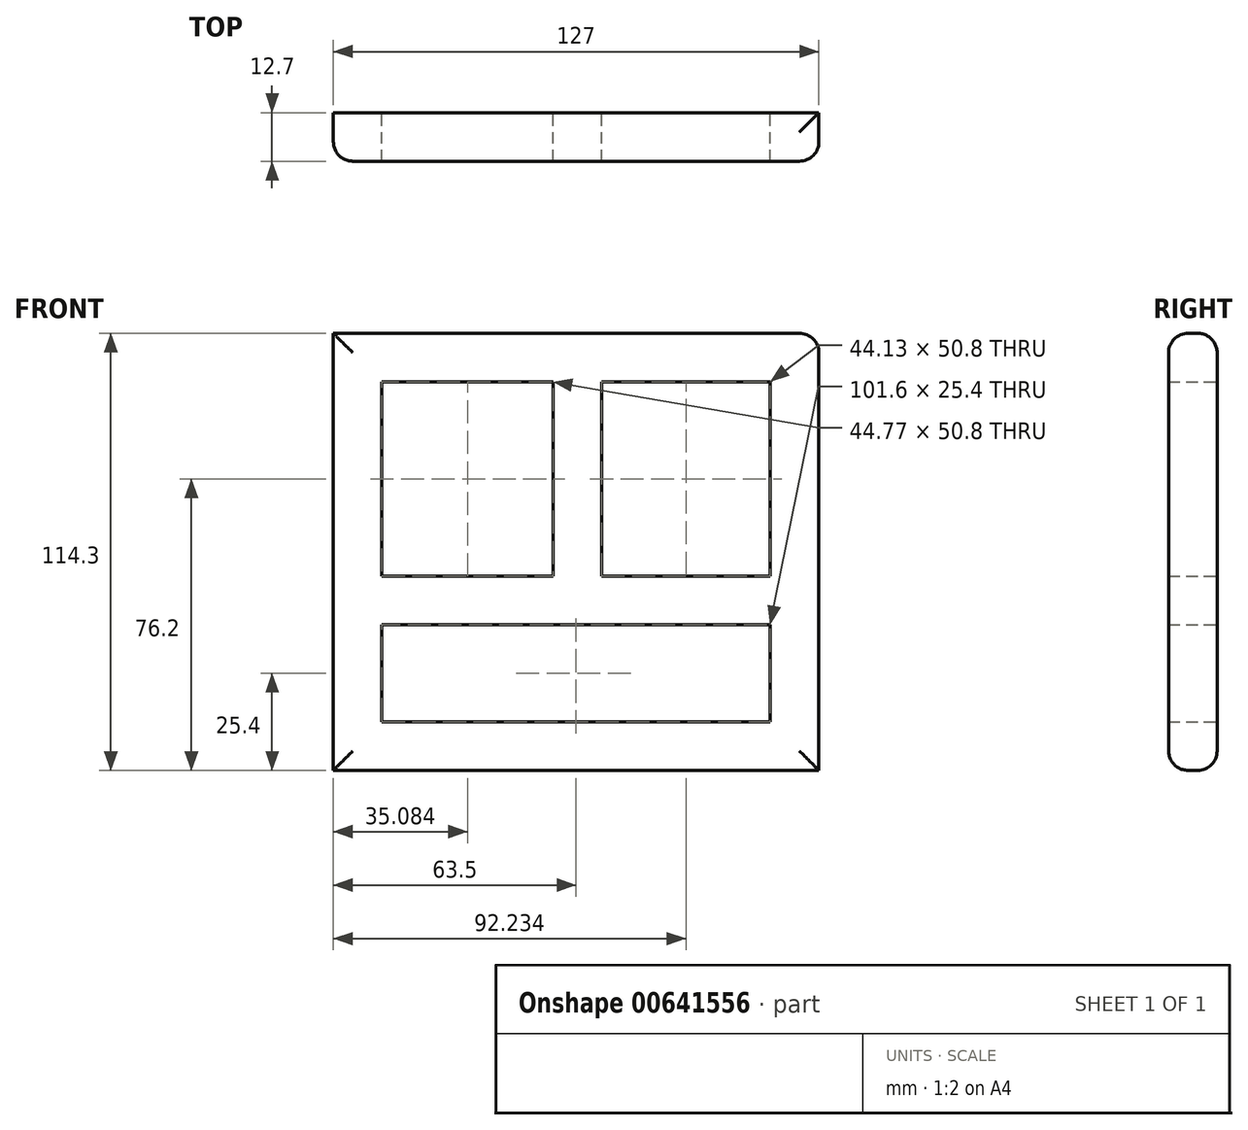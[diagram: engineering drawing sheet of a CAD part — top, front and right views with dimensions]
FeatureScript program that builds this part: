
annotation { "Feature Type Name" : "Feature", "Feature Type Description" : "" }
export const myFeature = defineFeature(function(context is Context, id is Id, definition is map)
    precondition{}
    {
        {
            var Q0;
            Q0=qCreatedBy(makeId("Front.planeOp"),FACE);
            var sketch = newSketch(context, id + "F0", { "sketchPlane" : qUnion([Q0])});
            skLineSegment(sketch, "E0.bottom", {"start": v(-63.5, -25.4) * mm, "end": v(63.5, -25.4) * mm});
            skLineSegment(sketch, "E0.top", {"start": v(-50.8, 25.4) * mm, "end": v(50.8, 25.4) * mm});
            skLineSegment(sketch, "E0.left", {"start": v(-63.5, -25.4) * mm, "end": v(-63.5, 25.4) * mm});
            skLineSegment(sketch, "E0.right", {"start": v(63.5, -25.4) * mm, "end": v(63.5, 25.4) * mm});
            skPoint(sketch, "E0.middle", {"position": v(0, 0) * mm});
            skLineSegment(sketch, "E1.bottom", {"start": v(-50.8, -12.7) * mm, "end": v(50.8, -12.7) * mm});
            skLineSegment(sketch, "E1.top", {"start": v(-50.8, 12.7) * mm, "end": v(50.8, 12.7) * mm});
            skLineSegment(sketch, "E1.left", {"start": v(-50.8, -12.7) * mm, "end": v(-50.8, 12.7) * mm});
            skLineSegment(sketch, "E1.right", {"start": v(50.8, -12.7) * mm, "end": v(50.8, 12.7) * mm});
            skLineSegment(sketch, "E2", {"start": v(-63.5, 25.4) * mm, "end": v(-63.5, 88.9) * mm});
            skLineSegment(sketch, "E3", {"start": v(-63.5, 88.9) * mm, "end": v(63.5, 88.9) * mm});
            skLineSegment(sketch, "E4", {"start": v(63.5, 88.9) * mm, "end": v(63.5, 25.4) * mm});
            skLineSegment(sketch, "E5", {"start": v(-50.8, 25.4) * mm, "end": v(-50.8, 76.2) * mm});
            skLineSegment(sketch, "E6", {"start": v(-50.8, 76.2) * mm, "end": v(50.8, 76.2) * mm});
            skLineSegment(sketch, "E7", {"start": v(50.8, 76.2) * mm, "end": v(50.8, 25.4) * mm});
            skLineSegment(sketch, "E8", {"start": v(-6.03, 25.4) * mm, "end": v(-6.03, 76.2) * mm});
            skLineSegment(sketch, "E9", {"start": v(-6.03, 76.2) * mm, "end": v(6.67, 76.2) * mm});
            skLineSegment(sketch, "E10", {"start": v(6.67, 76.2) * mm, "end": v(6.67, 25.4) * mm});
            skLineSegment(sketch, "E11", {"start": v(-50.8, 25.4) * mm, "end": v(-50.8, 12.7) * mm});
            skLineSegment(sketch, "E12", {"start": v(50.8, 25.4) * mm, "end": v(50.8, 12.7) * mm});
            skSolve(sketch);
        }
        {
            var Q0;
            Q0 = qSketchRegion(id + "F0", true);
            var Q1;
            Q1=makeQuery(id+"F0.imprint","IMPRINT",FACE,{"disambiguationData":[TD([[makeQuery(id+"F0.imprint","IMPRINT",EDGE,{"derivedFrom":sQuery(id+"F0.wireOp",EDGE,"E1.top")}),1.0]])]});
            var Q2;
            {var subQ0=sQuery(id+"F0.wireOp",EDGE,"E8");Q2=makeQuery(id+"F0.imprint","IMPRINT",FACE,{"disambiguationData":[TD([[makeQuery(id+"F0.imprint","IMPRINT",EDGE,{"derivedFrom":subQ0}),-1.0]])]});}
            extrude(context, id + "F1", {"entities" : qUnion([Q0, Q1, Q2]), "depth" : 12.7 * mm, "offsetDistance" : 25.4 * mm});
        }
        {
            var Q0;
            Q0=makeQuery(id+"F1.opExtrude","CAP_EDGE",EDGE,{"disambiguationData":[OSD([sQuery(id+"F0.wireOp",EDGE,"E3")])],"isStart":true});
            var Q1;
            Q1=makeQuery(id+"F1.opExtrude","CAP_EDGE",EDGE,{"disambiguationData":[OSD([sQuery(id+"F0.wireOp",EDGE,"E0.bottom")])],"isStart":true});
            var Q2;
            Q2=makeQuery(id+"F1.opExtrude","CAP_EDGE",EDGE,{"disambiguationData":[OSD([sQuery(id+"F0.wireOp",EDGE,"E0.right"),sQuery(id+"F0.wireOp",EDGE,"E4")])],"isStart":false});
            var Q3;
            Q3=makeQuery(id+"F1.opExtrude","SWEPT_EDGE",EDGE,{"disambiguationData":[OSD([sQuery(id+"F0.wireOp",EDGE,"E3"),sQuery(id+"F0.wireOp",EDGE,"E4")])]});
            var Q4;
            Q4=makeQuery(id+"F1.opExtrude","CAP_EDGE",EDGE,{"disambiguationData":[OSD([sQuery(id+"F0.wireOp",EDGE,"E3")])],"isStart":false});
            var Q5;
            Q5=makeQuery(id+"F1.opExtrude","CAP_EDGE",EDGE,{"disambiguationData":[OSD([sQuery(id+"F0.wireOp",EDGE,"E0.left"),sQuery(id+"F0.wireOp",EDGE,"E2")])],"isStart":false});
            var Q6;
            Q6=makeQuery(id+"F1.opExtrude","CAP_EDGE",EDGE,{"disambiguationData":[OSD([sQuery(id+"F0.wireOp",EDGE,"E0.bottom")])],"isStart":false});
            fillet(context, id + "F2", {"entities" : qUnion([Q0, Q1, Q2, Q3, Q4, Q5, Q6]), "radius" : 5.08 * mm, "tangentPropagation" : true, "allowEdgeOverflow" : false});
        }
    });
